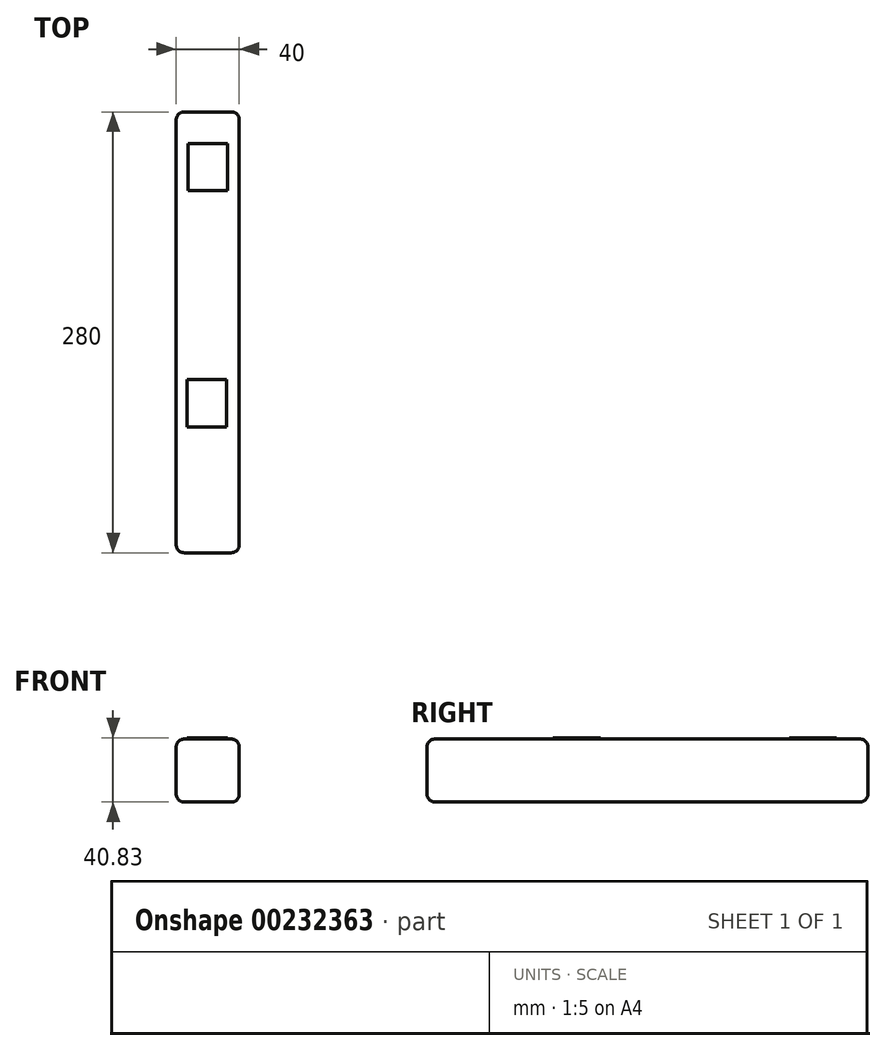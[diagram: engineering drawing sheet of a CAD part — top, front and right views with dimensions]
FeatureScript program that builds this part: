
annotation { "Feature Type Name" : "Feature", "Feature Type Description" : "" }
export const myFeature = defineFeature(function(context is Context, id is Id, definition is map)
    precondition{}
    {
        {
            var Q0;
            Q0=qCreatedBy(makeId("Front.planeOp"),FACE);
            var sketch = newSketch(context, id + "F0", { "sketchPlane" : qUnion([Q0])});
            skLineSegment(sketch, "E0.bottom", {"start": v(-20, 19.17) * mm, "end": v(20, 19.17) * mm});
            skLineSegment(sketch, "E0.top", {"start": v(-20, -20.83) * mm, "end": v(20, -20.83) * mm});
            skLineSegment(sketch, "E0.left", {"start": v(-20, 19.17) * mm, "end": v(-20, -20.83) * mm});
            skLineSegment(sketch, "E0.right", {"start": v(20, 19.17) * mm, "end": v(20, -20.83) * mm});
            skSolve(sketch);
        }
        {
            var Q0;
            Q0 = qSketchRegion(id + "F0", true);
            extrude(context, id + "F1", {"entities" : qUnion([Q0]), "depth" : 280 * mm});
        }
        {
            var Q0;
            Q0=qCreatedBy(makeId("Top.planeOp"),FACE);
            var sketch = newSketch(context, id + "F2", { "sketchPlane" : qUnion([Q0])});
            skLineSegment(sketch, "E1.bottom", {"start": v(-12.5, -20) * mm, "end": v(12.5, -20) * mm});
            skLineSegment(sketch, "E1.top", {"start": v(-12.5, -50) * mm, "end": v(12.5, -50) * mm});
            skLineSegment(sketch, "E1.left", {"start": v(-12.5, -20) * mm, "end": v(-12.5, -50) * mm});
            skLineSegment(sketch, "E1.right", {"start": v(12.5, -20) * mm, "end": v(12.5, -50) * mm});
            skLineSegment(sketch, "E2.direction1", {"start": v(12.5, -50) * mm, "end": v(37.5, -50) * mm, "construction": true});
            skLineSegment(sketch, "E3.0.1.0", {"start": v(-13.17, -170) * mm, "end": v(-13.17, -200) * mm});
            skLineSegment(sketch, "E3.0.1.1", {"start": v(-13.17, -200) * mm, "end": v(11.83, -200) * mm});
            skLineSegment(sketch, "E3.0.1.2", {"start": v(11.83, -170) * mm, "end": v(11.83, -200) * mm});
            skLineSegment(sketch, "E3.0.1.3", {"start": v(-13.17, -170) * mm, "end": v(11.83, -170) * mm});
            skLineSegment(sketch, "E3.direction1", {"start": v(-12.5, -50) * mm, "end": v(12.5, -50) * mm, "construction": true});
            skLineSegment(sketch, "E3.direction2", {"start": v(-12.5, -50) * mm, "end": v(-13.17, -200) * mm, "construction": true});
            skSolve(sketch);
        }
        {
            var Q0;
            Q0 = qSketchRegion(id + "F2", true);
            extrude(context, id + "F3", {"entities" : qUnion([Q0]), "operationType" : NewBodyOperationType.ADD, "depth" : 20 * mm});
        }
        {
            var Q0;
            Q0=makeQuery(id+"F1.opExtrude","CAP_FACE",FACE,{"disambiguationData":[OSD([sQuery(id+"F0.wireOp",EDGE,"E0.bottom"),sQuery(id+"F0.wireOp",EDGE,"E0.top"),sQuery(id+"F0.wireOp",EDGE,"E0.left"),sQuery(id+"F0.wireOp",EDGE,"E0.right")])],"isStart":true});
            var Q1;
            Q1=makeQuery(id+"F1.opExtrude","SWEPT_FACE",FACE,{"disambiguationData":[OSD([sQuery(id+"F0.wireOp",EDGE,"E0.right")])]});
            var Q2;
            Q2=makeQuery(id+"F1.opExtrude","SWEPT_FACE",FACE,{"disambiguationData":[OSD([sQuery(id+"F0.wireOp",EDGE,"E0.top")])]});
            var Q3;
            Q3=makeQuery(id+"F1.opExtrude","SWEPT_FACE",FACE,{"disambiguationData":[OSD([sQuery(id+"F0.wireOp",EDGE,"E0.left")])]});
            var Q4;
            Q4=makeQuery(id+"F1.opExtrude","CAP_FACE",FACE,{"disambiguationData":[OSD([sQuery(id+"F0.wireOp",EDGE,"E0.bottom"),sQuery(id+"F0.wireOp",EDGE,"E0.top"),sQuery(id+"F0.wireOp",EDGE,"E0.left"),sQuery(id+"F0.wireOp",EDGE,"E0.right")])],"isStart":false});
            fillet(context, id + "F4", {"entities" : qUnion([Q0, Q1, Q2, Q3, Q4]), "radius" : 5 * mm, "tangentPropagation" : true, "allowEdgeOverflow" : false});
        }
    });
